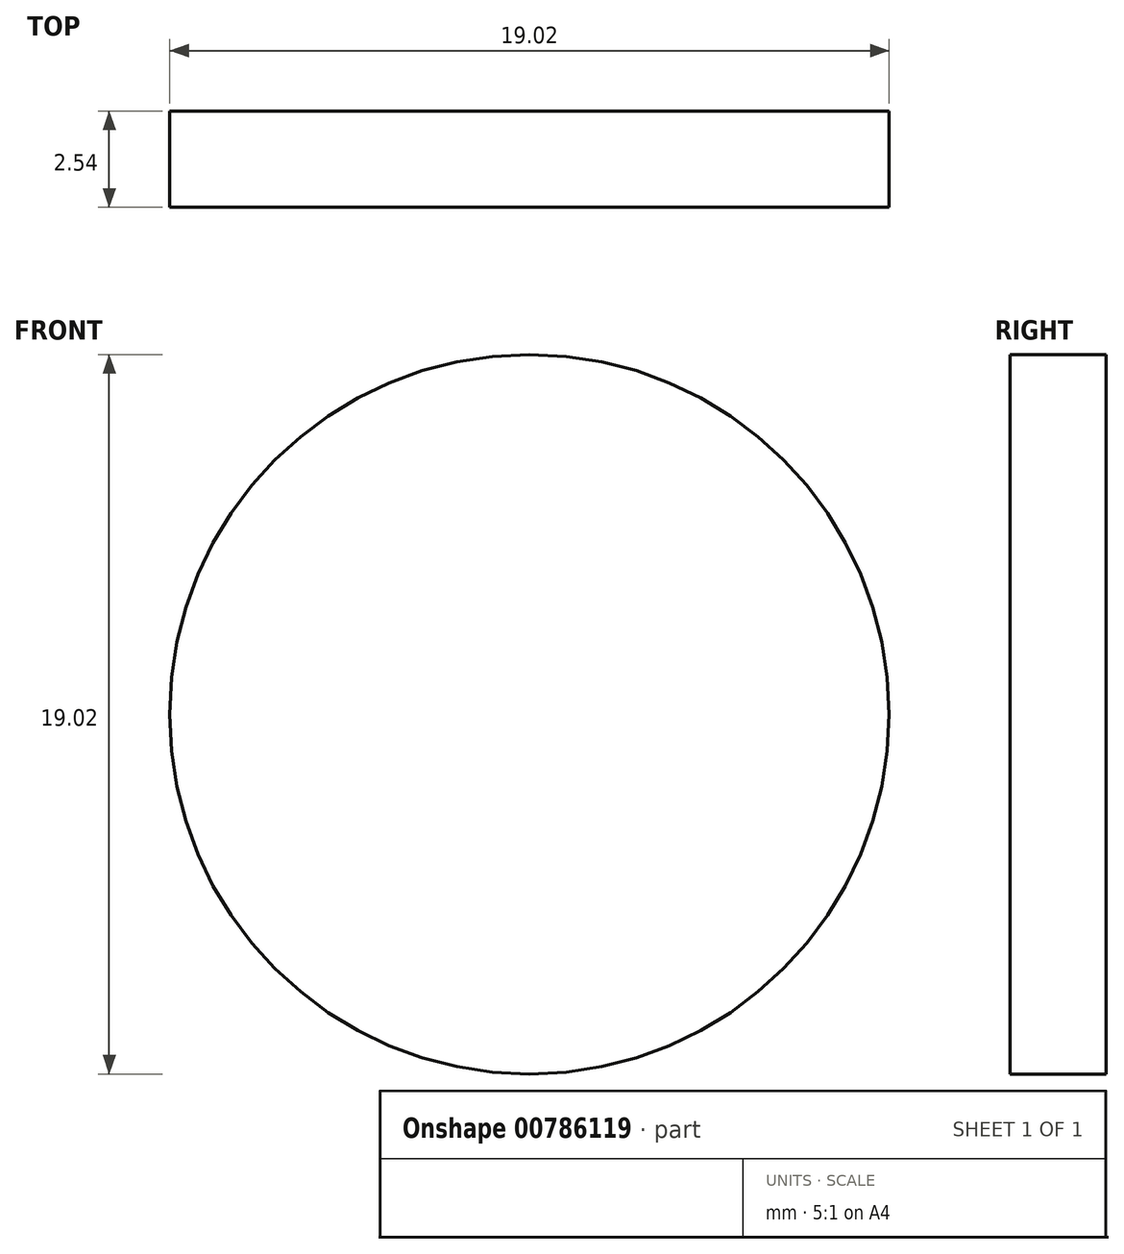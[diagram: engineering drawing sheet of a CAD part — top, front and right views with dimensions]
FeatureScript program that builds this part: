
annotation { "Feature Type Name" : "Feature", "Feature Type Description" : "" }
export const myFeature = defineFeature(function(context is Context, id is Id, definition is map)
    precondition{}
    {
        {
            var Q0;
            Q0=qCreatedBy(makeId("Front.planeOp"),FACE);
            var sketch = newSketch(context, id + "F0", { "sketchPlane" : qUnion([Q0])});
            skCircle(sketch, "E0", {"center": v(-37.1, 20) * mm, "radius": 9.51 * mm});
            skSolve(sketch);
        }
        {
            var Q0;
            Q0=makeQuery(id+"F0.imprint","IMPRINT",FACE,{"disambiguationData":[TD([[makeQuery(id+"F0.imprint","IMPRINT",EDGE,{"derivedFrom":sQuery(id+"F0.wireOp",EDGE,"E0")}),1.0]])]});
            extrude(context, id + "F1", {"entities" : qUnion([Q0]), "depth" : 2.54 * mm, "offsetDistance" : 25.4 * mm});
        }
    });
